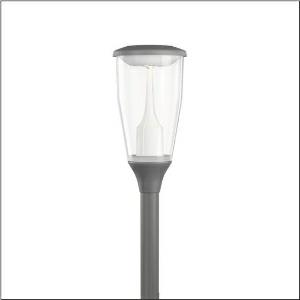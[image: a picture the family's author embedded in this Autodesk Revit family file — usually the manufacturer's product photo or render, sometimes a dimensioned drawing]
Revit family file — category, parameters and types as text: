
# Revit family: dl_11_iq___st1_2a_5xa5565af14hp00022_6a76
name_source: partatom
category: Lighting Fixtures
units: mm (PartAtom-declared; Revit-internal decimal feet)

## family parameters
Cut with Voids When Loaded = No
Host = Face
Light Source = No
Part Type = Normal
Room Calculation Point = No
Round Connector Dimension = Use Diameter
Shared = No

## types (1)
- --- (1 x LED, 4000 lm, 33.6 W, 2200K)
    Apparent Load = 34 VA
    CIE Flux Codes = 23 60 93 95 100
    Color Rendering = 70
    Color Temperature = 2200K
    Default Elevation = 1800 mm
    Description = DL 11 iQ, mast luminaire, Module 540 iQ-SR, primary light control with 3 zone facetted reflector, of plastic, silver coated, highly specular, structured, primary optical cover: cover, of PMMA, transparent, light distribution: ST1.2a, light emission: direct distribution, primary light characteristic: asymmetric, installation type: post-top, LED, High Power LED, light colour: 722, colour temperature: 2200K, control gear: iQ Street-Remote, control: Street-Remote, Auto-Match, Temp-Guard, Lumen-Switch, Night-Set, Smart-Wire, Light-Fading, Desk-Remote (wireless, voltage-free reading and setting of iQ features in the workshop via application-optimized NFC function/RFID function), optimised constant luminous flux control (CLO 2.0), mains connection: 220..240V, AC, 50/60Hz, connection cable pre-assembled, cable length: 5,5m, luminaire housing, upper part, of diecast aluminium, coated, Siteco® metallic grey (DB 702S), spigot size: 60mm (post-top), mounting height: 3..5m, post-top mast mounting element, of diecast aluminium, coated, Siteco® metallic grey (DB 702S), Module 540 iQ-SR, traffic white (RAL 9016), equipment: Power, protection rating (complete): IP66, insulation class (complete): insulation class II (safety insulation), certification: CE, ENEC, ENEC+, VDE, impact resistance: IK07, packaging unit: 1 piece

Light Distribution: ST1.2a
    Height = 665 mm
    Lamp = 1 x LED
    Lamp Light Flux = 4000 lm
    Lamp Power = 33.6 W
    Lamp count = 1
    Length = 334 mm
    Luminous efficacy = 119 lm/W
    Manufacturer = Siteco
    ModVariant = No
    Model = 5XA5565AF14HP00022
    Number of Poles = 1
    OnlyDefault = Yes
    Power Factor = 1
    Product Name = DL 11 iQ | ST1.2a
    Product group = mast luminaire | pylon top
    ProductGroupID = 6100
    Protection Class = Protection class II
    Protection Degree = IP 66
    RLX_Detail_Level = 1
    RLX_Emergency_Light_Flux = 0 lm
    RLX_Emergency_Type = 0
    RLX_Emergency_Type_DB = No
    RlxData = <blob elided: 141573 chars, md5=2e34282c>
    Socket = socket
    Standby Power = 0 W
    System Light Flux = 4000 lm
    System Power = 34 W
    Type Comments = factory setting: luminous flux: 100 % | dim-lin: 254 | 695 mA
    Type Image = l_1258354.jpg
    URL = http://relux.com
    VarID = @adj_053747
    Voltage = 0 V
    Weight = 0.00 kg
    Width = 0 mm  [stored 0 ft]

note: [stored X ft] marks values corroborated as IEEE doubles in the binary element streams (Revit-internal decimal feet)

## geometry (parser evidence)
native form markers: Blend x4, Sweep x9
no freeform markers — native parametric forms only
